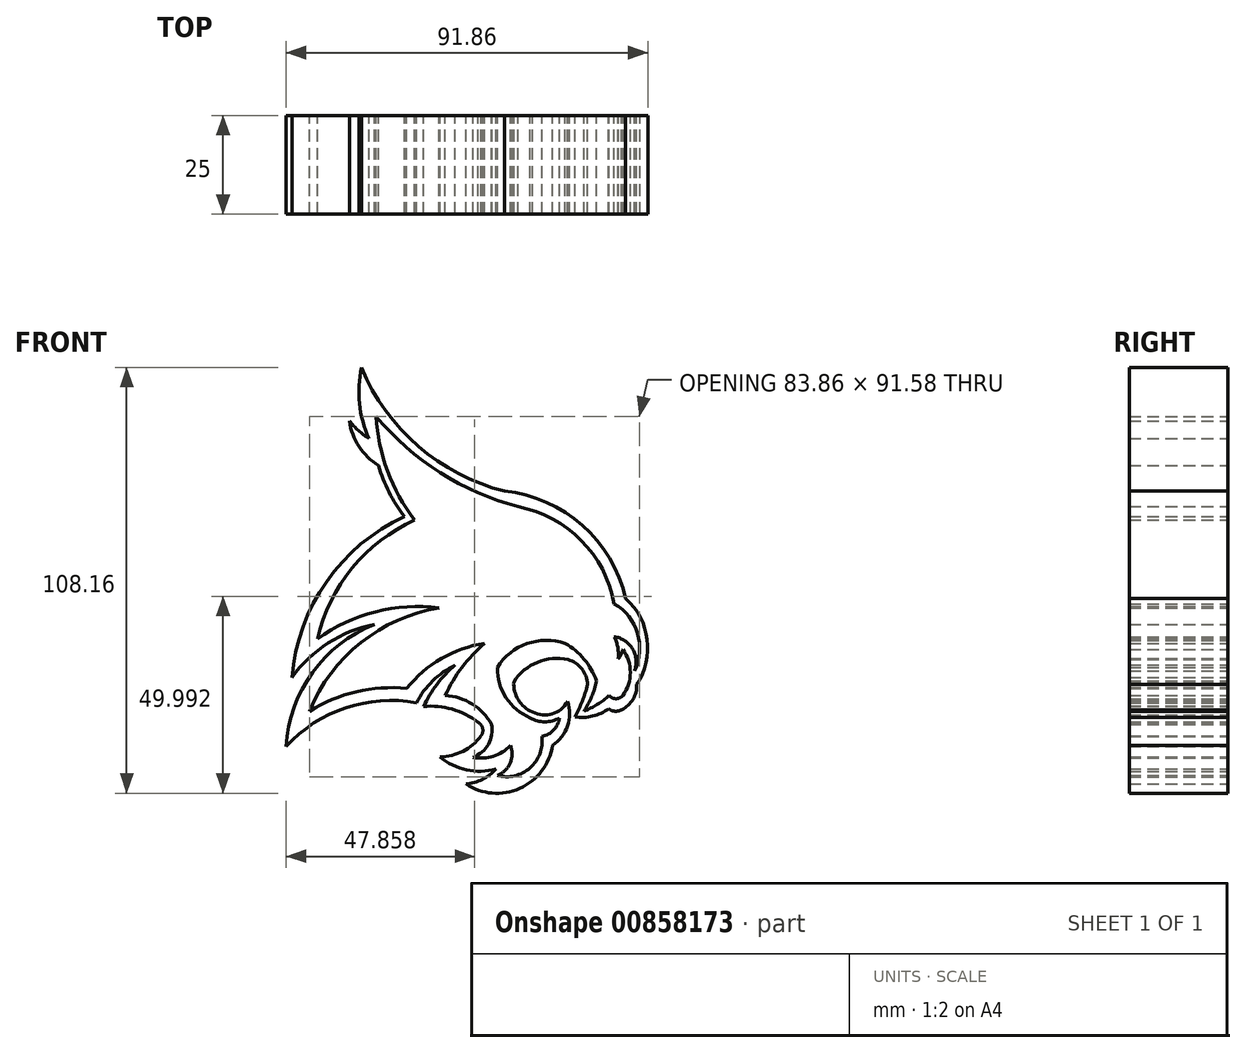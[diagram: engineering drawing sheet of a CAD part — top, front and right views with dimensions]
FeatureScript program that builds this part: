
annotation { "Feature Type Name" : "Feature", "Feature Type Description" : "" }
export const myFeature = defineFeature(function(context is Context, id is Id, definition is map)
    precondition{}
    {
        {
            var Q0;
            Q0=qCreatedBy(makeId("Front.planeOp"),FACE);
            var sketch = newSketch(context, id + "F0", { "sketchPlane" : qUnion([Q0])});
            skArc(sketch, "E0", {"start": v(-36.37, 62.11) * mm, "mid": v(-21.91, 42.1) * mm, "end": v(0, 30.7) * mm});
            skArc(sketch, "E1", {"start": v(30.74, 3.45) * mm, "mid": v(19.76, 22.02) * mm, "end": v(0, 30.7) * mm});
            skArc(sketch, "E2", {"start": v(33.55, -18.42) * mm, "mid": v(36.23, -6.97) * mm, "end": v(30.74, 3.45) * mm});
            skArc(sketch, "E3", {"start": v(29.7, -24.82) * mm, "mid": v(32.6, -22.2) * mm, "end": v(33.55, -18.42) * mm});
            skArc(sketch, "E4", {"start": v(26.44, -24.56) * mm, "mid": v(28.03, -25.2) * mm, "end": v(29.7, -24.82) * mm});
            skArc(sketch, "E5", {"start": v(17.87, -26.61) * mm, "mid": v(22.36, -26.47) * mm, "end": v(26.44, -24.56) * mm});
            skArc(sketch, "E6", {"start": v(17.87, -26.61) * mm, "mid": v(19.73, -22.62) * mm, "end": v(21.07, -18.42) * mm});
            skArc(sketch, "E7", {"start": v(21.07, -18.42) * mm, "mid": v(19.6, -14.45) * mm, "end": v(16.09, -12.08) * mm});
            skArc(sketch, "E8", {"start": v(16.09, -12.08) * mm, "mid": v(8.33, -12.77) * mm, "end": v(2.32, -17.72) * mm});
            skArc(sketch, "E9", {"start": v(2.32, -17.72) * mm, "mid": v(3.5, -22.3) * mm, "end": v(7.06, -25.4) * mm});
            skArc(sketch, "E10", {"start": v(7.06, -25.4) * mm, "mid": v(12.08, -25.88) * mm, "end": v(16.02, -22.7) * mm});
            skArc(sketch, "E11", {"start": v(12.18, -33.9) * mm, "mid": v(15.97, -28.95) * mm, "end": v(16.02, -22.7) * mm});
            skArc(sketch, "E12", {"start": v(-9.86, -43.72) * mm, "mid": v(3.83, -44.8) * mm, "end": v(12.18, -33.9) * mm});
            skArc(sketch, "E13", {"start": v(-9.86, -43.72) * mm, "mid": v(-5.66, -42.52) * mm, "end": v(-2.18, -39.88) * mm});
            skArc(sketch, "E14", {"start": v(-16.41, -36.8) * mm, "mid": v(-9.68, -40.13) * mm, "end": v(-2.18, -39.88) * mm});
            skArc(sketch, "E15", {"start": v(-16.41, -36.8) * mm, "mid": v(-10.6, -35.37) * mm, "end": v(-6.02, -31.5) * mm});
            skArc(sketch, "E16", {"start": v(-6.02, -31.5) * mm, "mid": v(-5.58, -29.6) * mm, "end": v(-6.78, -28.04) * mm});
            skArc(sketch, "E17", {"start": v(-6.78, -28.04) * mm, "mid": v(-13.31, -24.68) * mm, "end": v(-20.63, -24.01) * mm});
            skArc(sketch, "E18", {"start": v(-12.63, -13.5) * mm, "mid": v(-17.16, -18.36) * mm, "end": v(-20.63, -24.01) * mm});
            skArc(sketch, "E19", {"start": v(-12.63, -13.5) * mm, "mid": v(-18.27, -17.5) * mm, "end": v(-22.4, -23.07) * mm});
            skArc(sketch, "E20", {"start": v(-22.4, -23.07) * mm, "mid": v(-40.38, -24.33) * mm, "end": v(-55.5, -34.15) * mm});
            skArc(sketch, "E21", {"start": v(-33.08, -3.18) * mm, "mid": v(-48.82, -15.39) * mm, "end": v(-55.5, -34.15) * mm});
            skArc(sketch, "E22", {"start": v(-33.08, -3.18) * mm, "mid": v(-44.87, -7.9) * mm, "end": v(-54.05, -16.66) * mm});
            skArc(sketch, "E23", {"start": v(-25.46, 24.3) * mm, "mid": v(-45.26, 7.67) * mm, "end": v(-54.05, -16.66) * mm});
            skArc(sketch, "E24", {"start": v(-32, 37.22) * mm, "mid": v(-29.37, 30.44) * mm, "end": v(-25.46, 24.3) * mm});
            skArc(sketch, "E25", {"start": v(-39.45, 48.54) * mm, "mid": v(-36.98, 42.05) * mm, "end": v(-32, 37.22) * mm});
            skArc(sketch, "E26", {"start": v(-39.45, 48.54) * mm, "mid": v(-37.12, 46.1) * mm, "end": v(-34.46, 44.05) * mm});
            skArc(sketch, "E27", {"start": v(-36.37, 62.11) * mm, "mid": v(-36.87, 52.93) * mm, "end": v(-34.46, 44.05) * mm});
            skArc(sketch, "E28", {"start": v(-22.93, 34.57) * mm, "mid": v(-22.04, 30.44) * mm, "end": v(-19.88, 26.82) * mm});
            skArc(sketch, "E29", {"start": v(0, 23.86) * mm, "mid": v(-9.77, 26.45) * mm, "end": v(-19.88, 26.82) * mm});
            skArc(sketch, "E30", {"start": v(-22.93, 34.57) * mm, "mid": v(-17.5, 31.5) * mm, "end": v(-11.72, 29.17) * mm});
            skArc(sketch, "E31", {"start": v(0, 23.86) * mm, "mid": v(-5.72, 26.83) * mm, "end": v(-11.72, 29.17) * mm});
            skArc(sketch, "E32", {"start": v(17.03, 8.98) * mm, "mid": v(15.87, 4.66) * mm, "end": v(19.07, 1.54) * mm});
            skArc(sketch, "E33", {"start": v(19.07, 1.54) * mm, "mid": v(22.04, 2.04) * mm, "end": v(22.64, 5) * mm});
            skArc(sketch, "E34", {"start": v(19.39, 2.08) * mm, "mid": v(21.21, 3.32) * mm, "end": v(22.64, 5) * mm});
            skArc(sketch, "E35", {"start": v(19.39, 2.08) * mm, "mid": v(20.14, 4.54) * mm, "end": v(20.14, 7.12) * mm});
            skArc(sketch, "E36", {"start": v(20.14, 7.12) * mm, "mid": v(18.7, 8.22) * mm, "end": v(17.03, 8.98) * mm});
            skPoint(sketch, "E37.startSnap0", {"position": v(32.17, -14.97) * mm});
            skArc(sketch, "E38", {"start": v(-32.7, 49.73) * mm, "mid": v(-29.73, 35.82) * mm, "end": v(-22.87, 23.36) * mm});
            skArc(sketch, "E39", {"start": v(-22.87, 23.36) * mm, "mid": v(-38.72, 11.16) * mm, "end": v(-47.51, -6.8) * mm});
            skArc(sketch, "E40", {"start": v(-16.65, 1.04) * mm, "mid": v(-32.83, 0.04) * mm, "end": v(-47.51, -6.8) * mm});
            skArc(sketch, "E41", {"start": v(-16.65, 1.04) * mm, "mid": v(-36.54, -7.78) * mm, "end": v(-49.57, -25.2) * mm});
            skArc(sketch, "E42", {"start": v(-24.88, -19.4) * mm, "mid": v(-37.7, -20.26) * mm, "end": v(-49.57, -25.2) * mm});
            skArc(sketch, "E43", {"start": v(-5.08, -7.97) * mm, "mid": v(-16.05, -11.83) * mm, "end": v(-24.88, -19.4) * mm});
            skArc(sketch, "E44", {"start": v(-5.08, -7.97) * mm, "mid": v(-10.82, -14.04) * mm, "end": v(-15.1, -21.2) * mm});
            skArc(sketch, "E45", {"start": v(-3.28, -28.54) * mm, "mid": v(-8.26, -23.37) * mm, "end": v(-15.1, -21.2) * mm});
            skArc(sketch, "E46", {"start": v(-8.04, -36.9) * mm, "mid": v(-4.13, -33.59) * mm, "end": v(-3.28, -28.54) * mm});
            skArc(sketch, "E47", {"start": v(-8.04, -36.9) * mm, "mid": v(-2.9, -36.66) * mm, "end": v(1.48, -33.94) * mm});
            skArc(sketch, "E48", {"start": v(-1.87, -41.53) * mm, "mid": v(1.4, -38.43) * mm, "end": v(1.48, -33.94) * mm});
            skArc(sketch, "E49", {"start": v(-1.87, -41.53) * mm, "mid": v(6.46, -39.62) * mm, "end": v(9.45, -31.62) * mm});
            skArc(sketch, "E50", {"start": v(9.45, -31.62) * mm, "mid": v(12.46, -29.96) * mm, "end": v(13.95, -26.87) * mm});
            skArc(sketch, "E51", {"start": v(6.5, -26.87) * mm, "mid": v(10.22, -27.9) * mm, "end": v(13.95, -26.87) * mm});
            skArc(sketch, "E52", {"start": v(-1.87, -14.14) * mm, "mid": v(0.38, -21.77) * mm, "end": v(6.5, -26.87) * mm});
            skArc(sketch, "E53", {"start": v(15.36, -7.97) * mm, "mid": v(5.67, -8.05) * mm, "end": v(-1.87, -14.14) * mm});
            skArc(sketch, "E54", {"start": v(23.34, -17.48) * mm, "mid": v(20.2, -12) * mm, "end": v(15.36, -7.97) * mm});
            skArc(sketch, "E55", {"start": v(20.12, -25.2) * mm, "mid": v(22.12, -21.5) * mm, "end": v(23.34, -17.48) * mm});
            skArc(sketch, "E56", {"start": v(20.12, -25.2) * mm, "mid": v(23.52, -23.5) * mm, "end": v(26.55, -21.2) * mm});
            skArc(sketch, "E57", {"start": v(26.55, -21.2) * mm, "mid": v(28.29, -22.03) * mm, "end": v(30.02, -21.2) * mm});
            skArc(sketch, "E58", {"start": v(30.02, -21.2) * mm, "mid": v(31.94, -15.35) * mm, "end": v(30.02, -9.49) * mm});
            skArc(sketch, "E59", {"start": v(28.84, -11.94) * mm, "mid": v(29.6, -10.8) * mm, "end": v(30.02, -9.49) * mm});
            skArc(sketch, "E60", {"start": v(28.84, -11.94) * mm, "mid": v(28.76, -9.03) * mm, "end": v(27.85, -6.28) * mm});
            skArc(sketch, "E61", {"start": v(33, -15) * mm, "mid": v(32.51, -9.4) * mm, "end": v(27.85, -6.28) * mm});
            skArc(sketch, "E62", {"start": v(33, -15) * mm, "mid": v(33.77, -5.44) * mm, "end": v(27.85, 2.1) * mm});
            skArc(sketch, "E63", {"start": v(27.85, 2.1) * mm, "mid": v(19.45, 18.22) * mm, "end": v(3.4, 26.77) * mm});
            skArc(sketch, "E64", {"start": v(-32.7, 49.73) * mm, "mid": v(-16.43, 35.44) * mm, "end": v(3.4, 26.77) * mm});
            skSolve(sketch);
        }
        {
            var Q0;
            Q0 = qSketchRegion(id + "F0", true);
            extrude(context, id + "F1", {"entities" : qUnion([Q0]), "depth" : 25 * mm, "offsetDistance" : 25 * mm});
        }
    });
